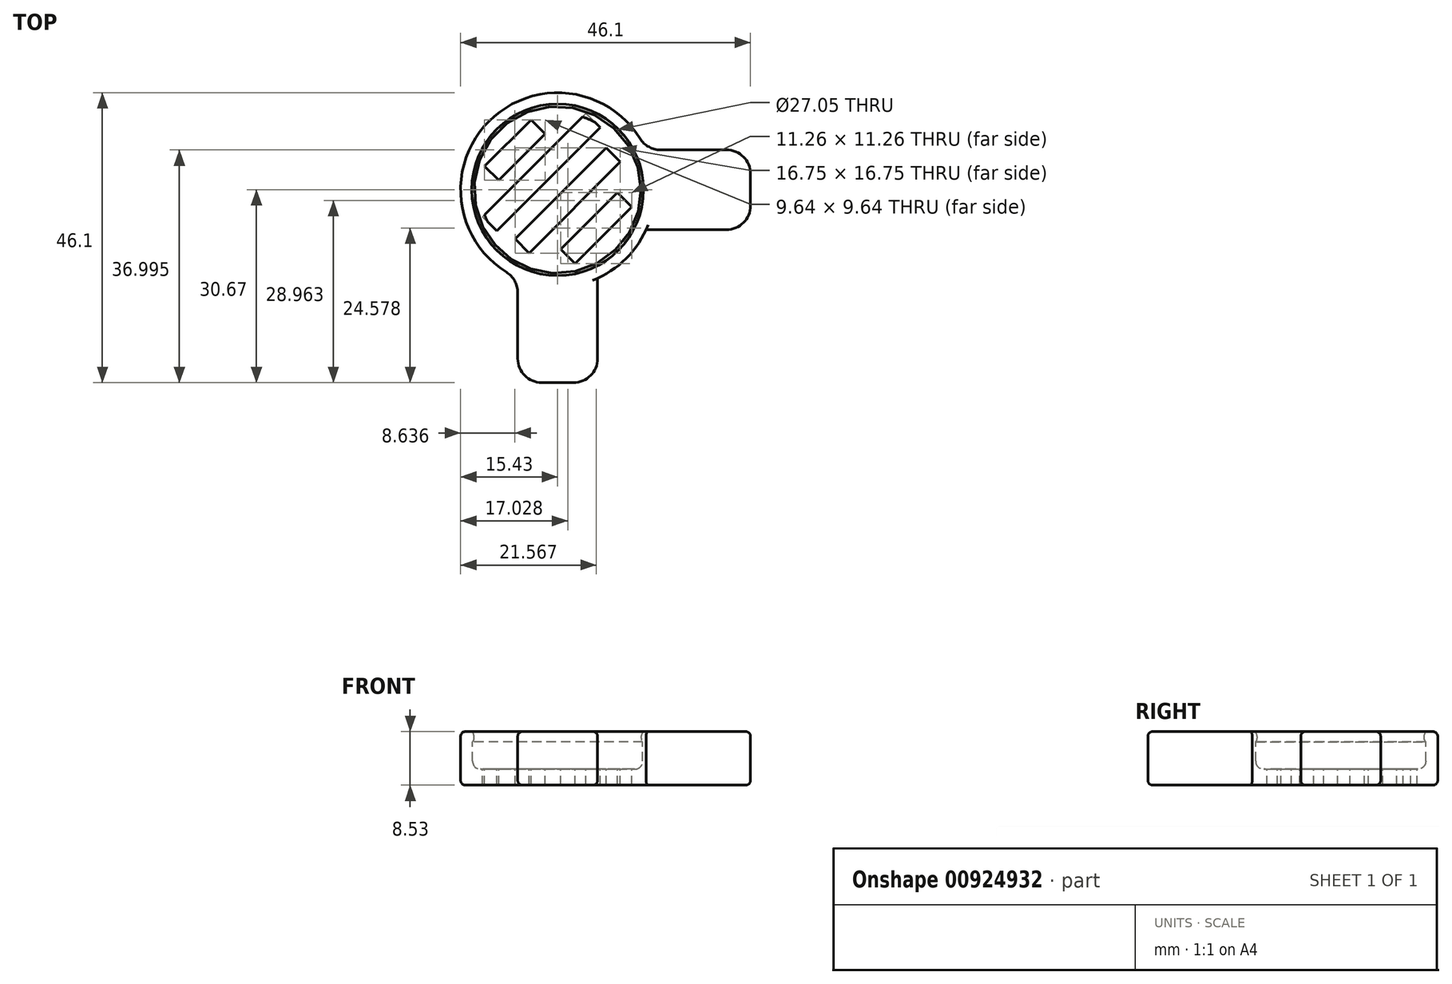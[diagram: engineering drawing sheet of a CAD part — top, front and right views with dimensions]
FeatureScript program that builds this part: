
annotation { "Feature Type Name" : "Feature", "Feature Type Description" : "" }
export const myFeature = defineFeature(function(context is Context, id is Id, definition is map)
    precondition{}
    {
        {
            var Q0;
            Q0=qCreatedBy(makeId("Front.planeOp"),FACE);
            var sketch = newSketch(context, id + "F0", { "sketchPlane" : qUnion([Q0])});
            skLineSegment(sketch, "E0", {"start": v(15.43, 6.71) * mm, "end": v(15.43, 0) * mm});
            skLineSegment(sketch, "E1", {"start": v(15.43, 0) * mm, "end": v(0, 0) * mm});
            skArc(sketch, "E2", {"start": v(15.43, 6.71) * mm, "mid": v(13.63, 6.73) * mm, "end": v(13.65, 8.53) * mm});
            skLineSegment(sketch, "E3", {"start": v(0, 10.9) * mm, "end": v(0, -2.45) * mm, "construction": true});
            skLineSegment(sketch, "E4", {"start": v(0, 0) * mm, "end": v(0, 2.54) * mm});
            skLineSegment(sketch, "E5", {"start": v(0, 2.54) * mm, "end": v(12.26, 2.54) * mm});
            skLineSegment(sketch, "E6", {"start": v(13.53, 3.81) * mm, "end": v(13.53, 6.86) * mm});
            skLineSegment(sketch, "E7", {"start": v(15.43, 6.71) * mm, "end": v(15.43, 8.53) * mm});
            skLineSegment(sketch, "E8", {"start": v(15.43, 8.53) * mm, "end": v(13.65, 8.53) * mm});
            skPoint(sketch, "E9.visualSharp", {"position": v(13.53, 2.54) * mm});
            skArc(sketch, "E10.filletArc", {"start": v(12.26, 2.54) * mm, "mid": v(13.15, 2.91) * mm, "end": v(13.53, 3.81) * mm});
            skPoint(sketch, "E11.visualSharp", {"position": v(15.43, 0) * mm});
            skPoint(sketch, "E12.visualSharp", {"position": v(15.43, 8.53) * mm});
            skSolve(sketch);
        }
        {
            var Q0;
            Q0=qSketchRegion(id+"F0",true);
            var Q1;
            Q1=sQuery(id+"F0.wireOp",EDGE,"E3");
            revolve(context, id + "F1", {"surfaceOperationType" : NewSurfaceOperationType.NEW, "entities" : qUnion([Q0]), "axis" : qUnion([Q1]), "revolveType" : RevolveType.FULL});
        }
        {
            var Q0;
            Q0=makeQuery(id+"F1.opRevolve","SWEPT_FACE",FACE,{"disambiguationData":[OSD([sQuery(id+"F0.wireOp",EDGE,"E8")])]});
            var sketch = newSketch(context, id + "F2", { "sketchPlane" : qUnion([Q0])});
            skLineSegment(sketch, "E13.bottom", {"start": v(30.67, 6.35) * mm, "end": v(14.06, 6.35) * mm});
            skLineSegment(sketch, "E13.top", {"start": v(30.67, -6.35) * mm, "end": v(14.06, -6.35) * mm});
            skLineSegment(sketch, "E13.left", {"start": v(30.67, 6.35) * mm, "end": v(30.67, -6.35) * mm});
            skLineSegment(sketch, "E14.bottom", {"start": v(6.35, -30.67) * mm, "end": v(-6.35, -30.67) * mm});
            skLineSegment(sketch, "E14.left", {"start": v(6.35, -30.67) * mm, "end": v(6.35, -14.06) * mm});
            skLineSegment(sketch, "E14.right", {"start": v(-6.35, -30.67) * mm, "end": v(-6.35, -14.06) * mm});
            skArc(sketch, "E15.0", {"start": v(-6.35, -14.06) * mm, "mid": v(0, -15.43) * mm, "end": v(6.35, -14.06) * mm});
            skArc(sketch, "E16.trimOffspring", {"start": v(14.06, -6.35) * mm, "mid": v(15.43, 0) * mm, "end": v(14.06, 6.35) * mm});
            skSolve(sketch);
        }
        {
            var Q0;
            Q0=qSketchRegion(id+"F2",true);
            var Q1;
            Q1=makeQuery(id+"F1.opRevolve","SWEPT_FACE",FACE,{"disambiguationData":[OSD([sQuery(id+"F0.wireOp",EDGE,"E1")])]});
            extrude(context, id + "F3", {"entities" : qUnion([Q0]), "operationType" : NewBodyOperationType.ADD, "endBound" : BoundingType.UP_TO_SURFACE, "oppositeDirection" : true, "depth" : 25.4 * mm, "endBoundEntityFace" : qUnion([Q1]), "offsetDistance" : 25.4 * mm});
        }
        {
            var Q0;
            Q0=makeQuery(id+"F3.opExtrude","SWEPT_EDGE",EDGE,{"disambiguationData":[OSD([sQuery(id+"F2.wireOp",EDGE,"E14.bottom"),sQuery(id+"F2.wireOp",EDGE,"E14.right")])]});
            var Q1;
            Q1=makeQuery(id+"F3.opExtrude","SWEPT_EDGE",EDGE,{"disambiguationData":[OSD([sQuery(id+"F0.wireOp",EDGE,"E7"),sQuery(id+"F0.wireOp",EDGE,"E8"),sQuery(id+"F2.wireOp",EDGE,"E14.right"),sQuery(id+"F2.wireOp",EDGE,"E15.0")])]});
            var Q2;
            Q2=makeQuery(id+"F3.opExtrude","SWEPT_EDGE",EDGE,{"disambiguationData":[OSD([sQuery(id+"F2.wireOp",EDGE,"E14.bottom"),sQuery(id+"F2.wireOp",EDGE,"E14.left")])]});
            var Q3;
            Q3=makeQuery(id+"F3.opExtrude","SWEPT_EDGE",EDGE,{"disambiguationData":[OSD([sQuery(id+"F0.wireOp",EDGE,"E7"),sQuery(id+"F0.wireOp",EDGE,"E8"),sQuery(id+"F2.wireOp",EDGE,"E14.left"),sQuery(id+"F2.wireOp",EDGE,"E15.0")])]});
            var Q4;
            Q4=makeQuery(id+"F3.opExtrude","SWEPT_EDGE",EDGE,{"disambiguationData":[OSD([sQuery(id+"F0.wireOp",EDGE,"E7"),sQuery(id+"F0.wireOp",EDGE,"E8"),sQuery(id+"F2.wireOp",EDGE,"E13.top"),sQuery(id+"F2.wireOp",EDGE,"E16.trimOffspring")])]});
            var Q5;
            Q5=makeQuery(id+"F3.opExtrude","SWEPT_EDGE",EDGE,{"disambiguationData":[OSD([sQuery(id+"F2.wireOp",EDGE,"E13.top"),sQuery(id+"F2.wireOp",EDGE,"E13.left")])]});
            var Q6;
            Q6=makeQuery(id+"F3.opExtrude","SWEPT_EDGE",EDGE,{"disambiguationData":[OSD([sQuery(id+"F2.wireOp",EDGE,"E13.bottom"),sQuery(id+"F2.wireOp",EDGE,"E13.left")])]});
            var Q7;
            Q7=makeQuery(id+"F3.opExtrude","SWEPT_EDGE",EDGE,{"disambiguationData":[OSD([sQuery(id+"F0.wireOp",EDGE,"E7"),sQuery(id+"F0.wireOp",EDGE,"E8"),sQuery(id+"F2.wireOp",EDGE,"E13.bottom"),sQuery(id+"F2.wireOp",EDGE,"E16.trimOffspring")])]});
            fillet(context, id + "F4", {"entities" : qUnion([Q0, Q1, Q2, Q3, Q4, Q5, Q6, Q7]), "radius" : 3.8 * mm, "tangentPropagation" : true, "allowEdgeOverflow" : false});
        }
        {
            var Q0;
            Q0=makeQuery(id+"F3.opExtrude","CAP_EDGE",EDGE,{"disambiguationData":[OSD([sQuery(id+"F2.wireOp",EDGE,"E14.bottom")])],"isStart":true});
            var Q1;
            Q1=makeQuery(id+"F3.opExtrude","CAP_EDGE",EDGE,{"disambiguationData":[OSD([sQuery(id+"F2.wireOp",EDGE,"E14.bottom")])],"isStart":false});
            fillet(context, id + "F5", {"entities" : qUnion([Q0, Q1]), "radius" : 0.76 * mm, "tangentPropagation" : true, "allowEdgeOverflow" : false});
        }
        {
            var Q0;
            Q0=makeQuery(id+"F1.opRevolve","SWEPT_FACE",FACE,{"disambiguationData":[OSD([sQuery(id+"F0.wireOp",EDGE,"E5")])]});
            var sketch = newSketch(context, id + "F6", { "sketchPlane" : qUnion([Q0])});
            skLineSegment(sketch, "E17", {"start": v(11.77, -2.7) * mm, "end": v(2.75, -11.72) * mm});
            skLineSegment(sketch, "E18", {"start": v(2.75, -11.72) * mm, "end": v(0.5, -9.48) * mm});
            skLineSegment(sketch, "E19", {"start": v(0.5, -9.48) * mm, "end": v(9.52, -0.46) * mm});
            skLineSegment(sketch, "E20", {"start": v(9.52, -0.46) * mm, "end": v(11.77, -2.7) * mm});
            skLineSegment(sketch, "E21", {"start": v(9.97, 4.42) * mm, "end": v(-4.53, -10.08) * mm});
            skLineSegment(sketch, "E22", {"start": v(-4.53, -10.08) * mm, "end": v(-6.78, -7.84) * mm});
            skLineSegment(sketch, "E23", {"start": v(-6.78, -7.84) * mm, "end": v(7.73, 6.67) * mm});
            skLineSegment(sketch, "E24", {"start": v(7.73, 6.67) * mm, "end": v(9.97, 4.42) * mm});
            skLineSegment(sketch, "E25", {"start": v(6.76, 9.9) * mm, "end": v(-9.68, -6.54) * mm});
            skLineSegment(sketch, "E26", {"start": v(-9.68, -6.54) * mm, "end": v(-11.93, -4.3) * mm});
            skLineSegment(sketch, "E27", {"start": v(-11.93, -4.3) * mm, "end": v(4.51, 12.15) * mm});
            skLineSegment(sketch, "E28", {"start": v(4.51, 12.15) * mm, "end": v(6.76, 9.9) * mm});
            skLineSegment(sketch, "E29", {"start": v(-1.97, 8.9) * mm, "end": v(-9.37, 1.5) * mm});
            skLineSegment(sketch, "E30", {"start": v(-9.37, 1.5) * mm, "end": v(-11.61, 3.75) * mm});
            skLineSegment(sketch, "E31", {"start": v(-11.61, 3.75) * mm, "end": v(-4.22, 11.14) * mm});
            skLineSegment(sketch, "E32", {"start": v(-4.22, 11.14) * mm, "end": v(-1.97, 8.9) * mm});
            skSolve(sketch);
        }
        {
            var Q0;
            Q0 = qSketchRegion(id + "F6", true);
            extrude(context, id + "F7", {"entities" : qUnion([Q0]), "operationType" : NewBodyOperationType.REMOVE, "oppositeDirection" : true, "depth" : 25.4 * mm, "offsetDistance" : 25.4 * mm});
        }
    });
